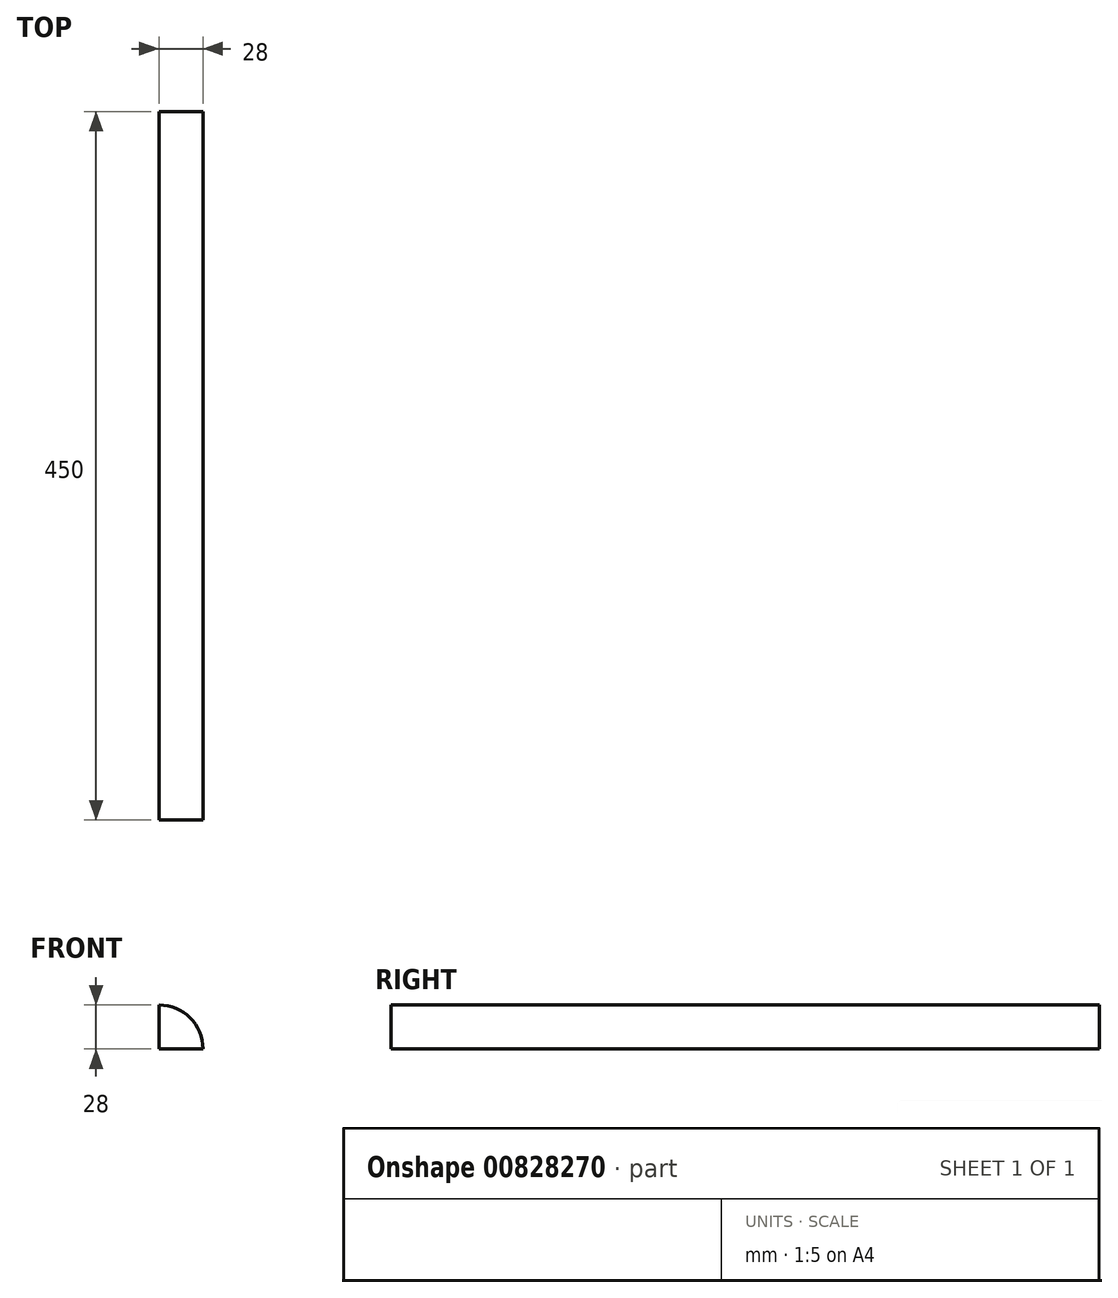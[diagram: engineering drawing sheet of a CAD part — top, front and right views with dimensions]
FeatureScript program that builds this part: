
annotation { "Feature Type Name" : "Feature", "Feature Type Description" : "" }
export const myFeature = defineFeature(function(context is Context, id is Id, definition is map)
    precondition{}
    {
        {
            var Q0;
            Q0=qCreatedBy(makeId("Front.planeOp"),FACE);
            var sketch = newSketch(context, id + "F0", { "sketchPlane" : qUnion([Q0])});
            skLineSegment(sketch, "E0", {"start": v(28, 0) * mm, "end": v(0, 0) * mm});
            skLineSegment(sketch, "E1", {"start": v(0, 0) * mm, "end": v(0, 28) * mm});
            skArc(sketch, "E2", {"start": v(28, 0) * mm, "mid": v(19.8, 19.8) * mm, "end": v(0, 28) * mm});
            skSolve(sketch);
        }
        {
            var Q0;
            Q0=makeQuery(id+"F0.imprint","IMPRINT",FACE,{"disambiguationData":[TD([[makeQuery(id+"F0.imprint","IMPRINT",EDGE,{"derivedFrom":sQuery(id+"F0.wireOp",EDGE,"E0")}),-1.0]])]});
            extrude(context, id + "F1", {"entities" : qUnion([Q0]), "endBound" : BoundingType.SYMMETRIC, "depth" : 450 * mm, "offsetDistance" : 25 * mm});
        }
    });
